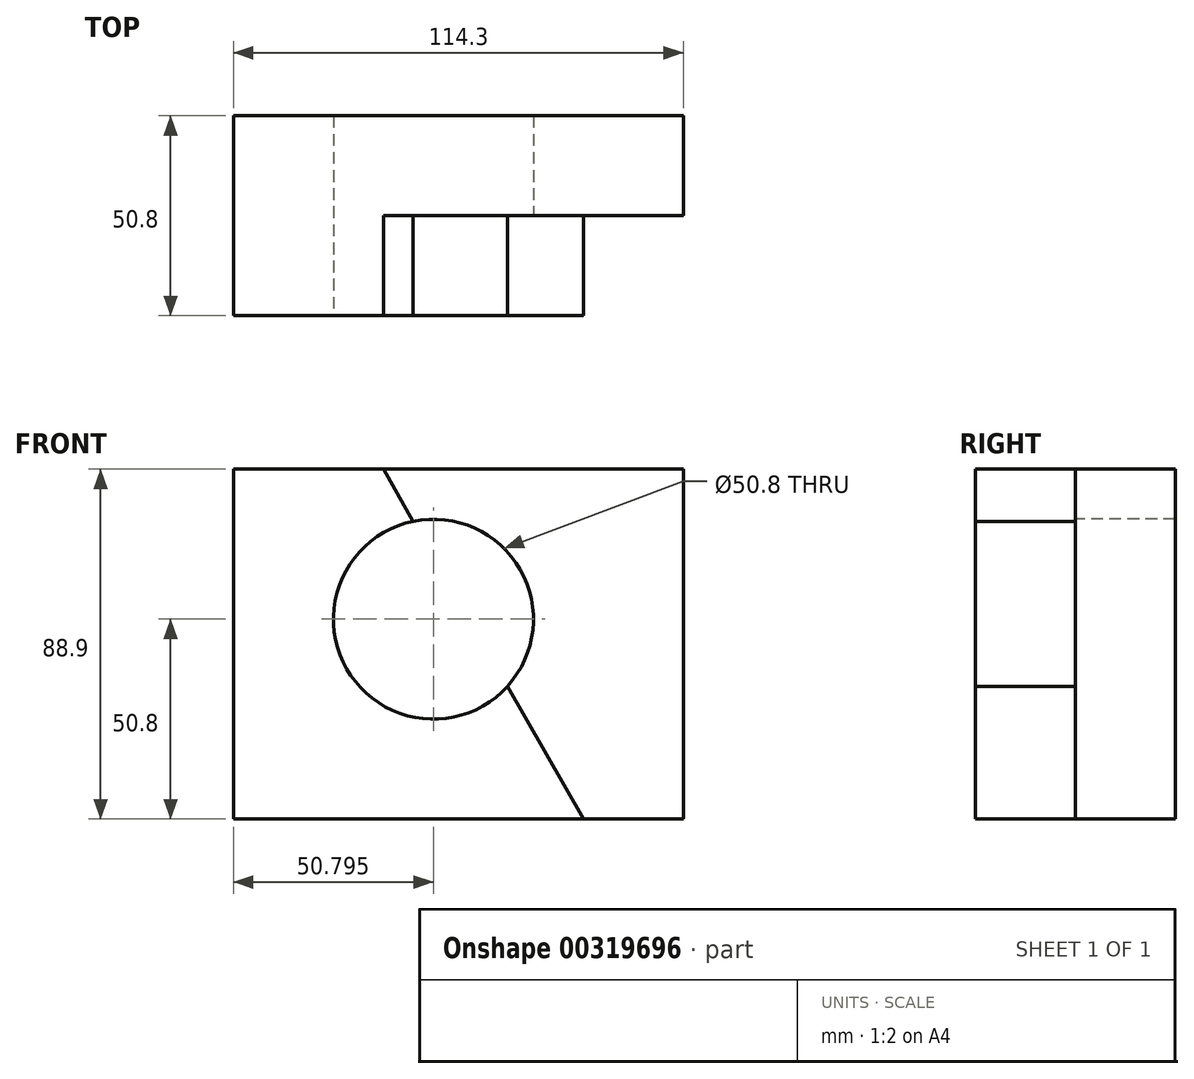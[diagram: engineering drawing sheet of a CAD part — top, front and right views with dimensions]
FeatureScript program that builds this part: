
annotation { "Feature Type Name" : "Feature", "Feature Type Description" : "" }
export const myFeature = defineFeature(function(context is Context, id is Id, definition is map)
    precondition{}
    {
        {
            var Q0;
            Q0=qCreatedBy(makeId("Top.planeOp"),FACE);
            var sketch = newSketch(context, id + "F0", { "sketchPlane" : qUnion([Q0])});
            skLineSegment(sketch, "E0", {"start": v(-47.06, 20.12) * mm, "end": v(-47.06, -30.68) * mm});
            skLineSegment(sketch, "E1", {"start": v(-47.06, 20.12) * mm, "end": v(67.24, 20.12) * mm});
            skLineSegment(sketch, "E2", {"start": v(-47.06, -30.68) * mm, "end": v(67.24, -30.68) * mm});
            skLineSegment(sketch, "E3", {"start": v(67.24, -30.68) * mm, "end": v(67.24, 20.12) * mm});
            skSolve(sketch);
        }
        {
            var Q0;
            Q0 = qSketchRegion(id + "F0", true);
            extrude(context, id + "F1", {"entities" : qUnion([Q0]), "depth" : 88.9 * mm});
        }
        {
            var Q0;
            Q0=makeQuery(id+"F1.opExtrude","SWEPT_FACE",FACE,{"disambiguationData":[OSD([sQuery(id+"F0.wireOp",EDGE,"E2")])]});
            var sketch = newSketch(context, id + "F2", { "sketchPlane" : qUnion([Q0])});
            skLineSegment(sketch, "E4", {"start": v(67.24, 0) * mm, "end": v(41.84, 0) * mm});
            skLineSegment(sketch, "E5", {"start": v(-8.96, 88.9) * mm, "end": v(41.84, 0) * mm});
            skSolve(sketch);
        }
        {
            var Q0;
            Q0=makeQuery(id+"F2.imprint","IMPRINT",FACE,{"disambiguationData":[TD([[makeQuery(id+"F2.imprint","IMPRINT",EDGE,{"derivedFrom":sQuery(id+"F2.wireOp",EDGE,"E4")}),1.0]])]});
            extrude(context, id + "F3", {"entities" : qUnion([Q0]), "operationType" : NewBodyOperationType.REMOVE, "oppositeDirection" : true, "depth" : 25.4 * mm});
        }
        {
            var Q0;
            Q0=makeQuery(id+"F1.opExtrude","SWEPT_FACE",FACE,{"disambiguationData":[OSD([sQuery(id+"F0.wireOp",EDGE,"E2")])]});
            var sketch = newSketch(context, id + "F4", { "sketchPlane" : qUnion([Q0])});
            skCircle(sketch, "E6", {"center": v(3.74, 50.8) * mm, "radius": 25.4 * mm});
            skSolve(sketch);
        }
        {
            var Q0;
            {var subQ0=sQuery(id+"F4.wireOp",EDGE,"E6");var subQ1=makeQuery(id+"F3.boolean.opBoolean","COPY",EDGE,{"derivedFrom":makeQuery(id+"F3.opExtrude","CAP_EDGE",EDGE,{"disambiguationData":[OSD([sQuery(id+"F2.wireOp",EDGE,"E5")])],"isStart":true})});var subQ2=makeQuery(id+"F4.imprint","INTERSECT",VERTEX,{"disambiguationData":[OD(0.0)],"derivedFrom":[subQ1,subQ0]});Q0=makeQuery(id+"F4.imprint","IMPRINT",FACE,{"disambiguationData":[TD([[makeQuery(id+"F4.imprint","IMPRINT",EDGE,{"disambiguationData":[TD([[subQ2,-1.0]])],"derivedFrom":subQ0}),1.0]])]});}
            var Q1;
            {var subQ0=sQuery(id+"F4.wireOp",EDGE,"E6");var subQ1=makeQuery(id+"F3.boolean.opBoolean","COPY",EDGE,{"derivedFrom":makeQuery(id+"F3.opExtrude","CAP_EDGE",EDGE,{"disambiguationData":[OSD([sQuery(id+"F2.wireOp",EDGE,"E5")])],"isStart":true})});var subQ2=makeQuery(id+"F4.imprint","INTERSECT",VERTEX,{"disambiguationData":[OD(0.0)],"derivedFrom":[subQ1,subQ0]});Q1=makeQuery(id+"F4.imprint","IMPRINT",FACE,{"disambiguationData":[TD([[makeQuery(id+"F4.imprint","IMPRINT",EDGE,{"disambiguationData":[TD([[subQ2,1.0]])],"derivedFrom":subQ0}),1.0]])]});}
            extrude(context, id + "F5", {"entities" : qUnion([Q0, Q1]), "operationType" : NewBodyOperationType.REMOVE, "endBound" : BoundingType.THROUGH_ALL, "oppositeDirection" : true, "depth" : 25.4 * mm});
        }
    });
